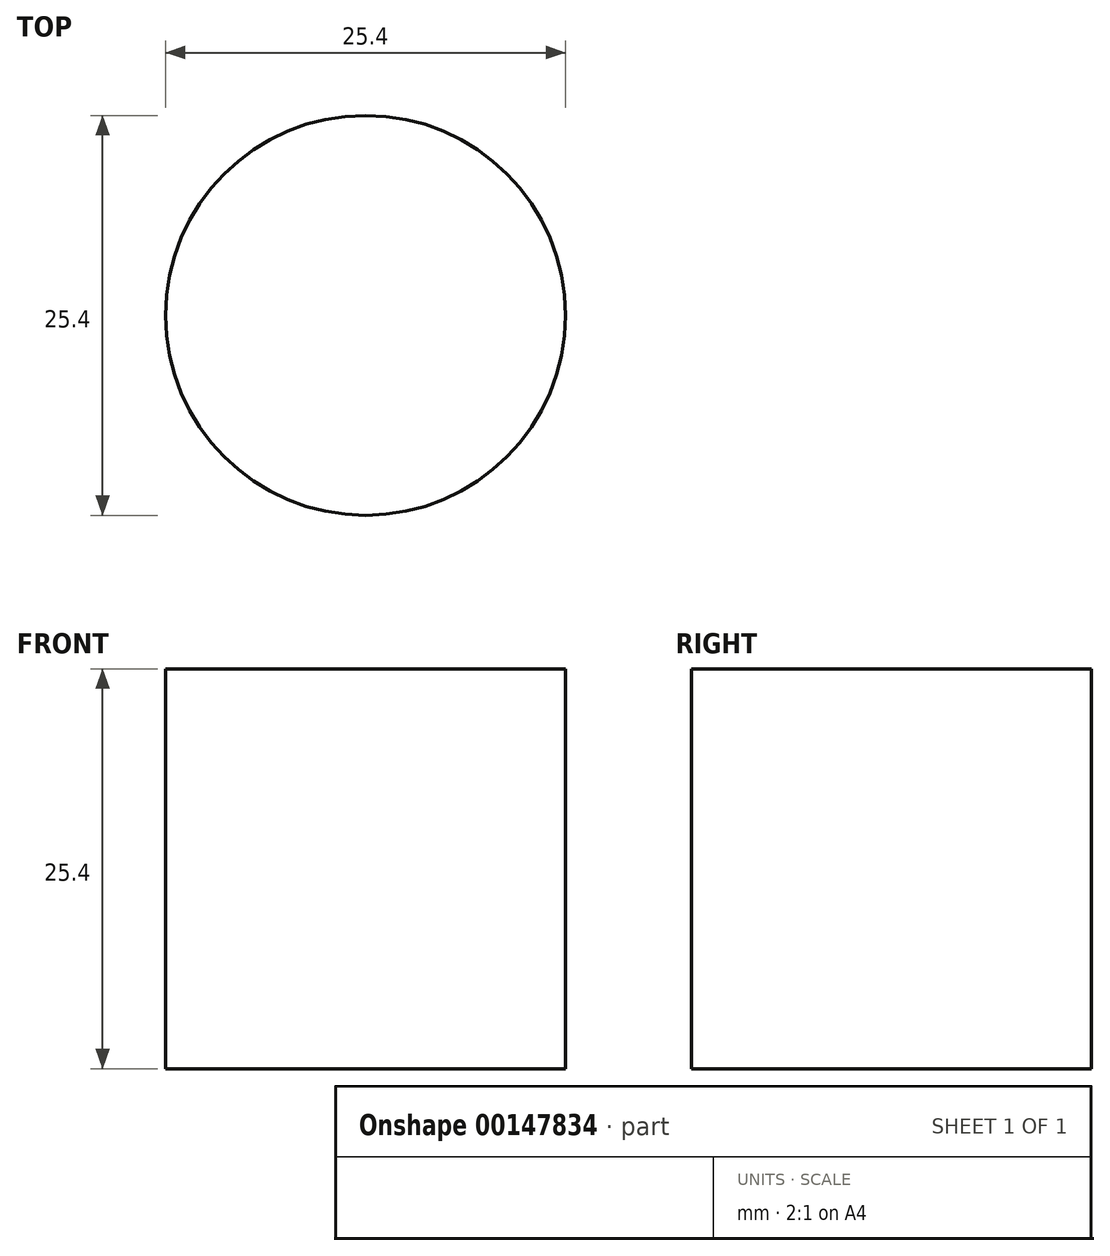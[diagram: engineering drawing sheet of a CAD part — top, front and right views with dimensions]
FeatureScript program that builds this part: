
annotation { "Feature Type Name" : "Feature", "Feature Type Description" : "" }
export const myFeature = defineFeature(function(context is Context, id is Id, definition is map)
    precondition{}
    {
        {
            var Q0;
            Q0=qCreatedBy(makeId("Top.planeOp"),FACE);
            var sketch = newSketch(context, id + "F0", { "sketchPlane" : qUnion([Q0])});
            skLineSegment(sketch, "E0.bottom", {"start": v(0, 0) * mm, "end": v(442.41, 0) * mm, "construction": true});
            skLineSegment(sketch, "E0.top", {"start": v(0, 304.8) * mm, "end": v(442.41, 304.8) * mm, "construction": true});
            skLineSegment(sketch, "E0.left", {"start": v(0, 0) * mm, "end": v(0, 304.8) * mm, "construction": true});
            skLineSegment(sketch, "E0.right", {"start": v(442.41, 0) * mm, "end": v(442.41, 304.8) * mm, "construction": true});
            skLineSegment(sketch, "E1", {"start": v(442.41, 152.4) * mm, "end": v(339.77, 152.4) * mm, "construction": true});
            skLineSegment(sketch, "E2", {"start": v(339.77, 152.4) * mm, "end": v(339.77, 457.2) * mm, "construction": true});
            skLineSegment(sketch, "E3", {"start": v(339.77, 457.2) * mm, "end": v(450.32, 956.45) * mm, "construction": true});
            skLineSegment(sketch, "E4", {"start": v(450.32, 956.45) * mm, "end": v(869.41, 1249.43) * mm, "construction": true});
            skLineSegment(sketch, "E5", {"start": v(869.41, 1249.43) * mm, "end": v(869.41, 1101.6) * mm, "construction": true});
            skLineSegment(sketch, "E6.bottom", {"start": v(888.46, 1101.6) * mm, "end": v(888.46, 1025.4) * mm, "construction": true});
            skLineSegment(sketch, "E6.top", {"start": v(850.36, 1101.6) * mm, "end": v(850.36, 1025.4) * mm, "construction": true});
            skLineSegment(sketch, "E6.left", {"start": v(888.46, 1101.6) * mm, "end": v(850.36, 1101.6) * mm, "construction": true});
            skLineSegment(sketch, "E6.right", {"start": v(888.46, 1025.4) * mm, "end": v(850.36, 1025.4) * mm, "construction": true});
            skLineSegment(sketch, "E7", {"start": v(869.41, 1025.4) * mm, "end": v(869.41, 1000) * mm, "construction": true});
            skLineSegment(sketch, "E8.bottom", {"start": v(885.29, 1000) * mm, "end": v(885.29, 961.9) * mm, "construction": true});
            skLineSegment(sketch, "E8.top", {"start": v(853.54, 1000) * mm, "end": v(853.54, 961.9) * mm, "construction": true});
            skLineSegment(sketch, "E8.left", {"start": v(885.29, 1000) * mm, "end": v(853.54, 1000) * mm, "construction": true});
            skLineSegment(sketch, "E8.right", {"start": v(885.29, 961.9) * mm, "end": v(853.54, 961.9) * mm, "construction": true});
            skLineSegment(sketch, "E9.bottom", {"start": v(569.41, 1000) * mm, "end": v(569.41, 900) * mm, "construction": true});
            skLineSegment(sketch, "E9.top", {"start": v(1169.41, 1000) * mm, "end": v(1169.41, 900) * mm, "construction": true});
            skLineSegment(sketch, "E9.right", {"start": v(569.41, 900) * mm, "end": v(1169.41, 900) * mm, "construction": true});
            skLineSegment(sketch, "E10", {"start": v(885.29, 1000) * mm, "end": v(1169.41, 1000) * mm, "construction": true});
            skLineSegment(sketch, "E11", {"start": v(853.54, 1000) * mm, "end": v(569.41, 1000) * mm, "construction": true});
            skCircle(sketch, "E12", {"center": v(0, 0) * mm, "radius": 12.7 * mm});
            skLineSegment(sketch, "E13", {"start": v(339.77, 457.2) * mm, "end": v(354.43, 431.8) * mm, "construction": true});
            skLineSegment(sketch, "E14", {"start": v(339.77, 457.2) * mm, "end": v(325.1, 431.8) * mm, "construction": true});
            skLineSegment(sketch, "E15", {"start": v(325.1, 431.8) * mm, "end": v(354.43, 431.8) * mm, "construction": true});
            skPoint(sketch, "E16", {"position": v(339.77, 431.8) * mm});
            skLineSegment(sketch, "E17", {"start": v(450.32, 956.45) * mm, "end": v(459.14, 928.48) * mm, "construction": true});
            skLineSegment(sketch, "E18", {"start": v(450.32, 956.45) * mm, "end": v(430.5, 934.82) * mm, "construction": true});
            skLineSegment(sketch, "E19", {"start": v(430.5, 934.82) * mm, "end": v(459.14, 928.48) * mm, "construction": true});
            skPoint(sketch, "E20", {"position": v(444.83, 931.65) * mm});
            skLineSegment(sketch, "E21", {"start": v(869.41, 1249.43) * mm, "end": v(857, 1222.86) * mm, "construction": true});
            skLineSegment(sketch, "E22", {"start": v(857, 1222.86) * mm, "end": v(840.2, 1246.9) * mm, "construction": true});
            skLineSegment(sketch, "E23", {"start": v(840.2, 1246.9) * mm, "end": v(869.41, 1249.43) * mm, "construction": true});
            skPoint(sketch, "E24", {"position": v(848.6, 1234.88) * mm});
            skCircle(sketch, "E25", {"center": v(442.41, 304.8) * mm, "radius": 32.54 * mm, "construction": true});
            skLineSegment(sketch, "E26", {"start": v(442.41, 0) * mm, "end": v(569.41, 0) * mm, "construction": true});
            skLineSegment(sketch, "E27", {"start": v(569.41, 900) * mm, "end": v(569.41, 0) * mm, "construction": true});
            skCircle(sketch, "E28", {"center": v(569.41, 1000) * mm, "radius": 32.54 * mm, "construction": true});
            skSolve(sketch);
        }
        {
            var Q0;
            Q0=qSketchRegion(id+"F0",true);
            extrude(context, id + "F1", {"entities" : qUnion([Q0]), "depth" : 25.4 * mm});
        }
    });
